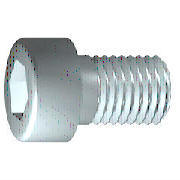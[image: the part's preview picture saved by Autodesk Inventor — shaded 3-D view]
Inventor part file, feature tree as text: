
AUTODESK INVENTOR PART (.ipt)
format: ipt  version: 2020 (Build 240168000, 168)  size: 196,608 bytes
history: native  units: mm (DEFAULTED — no unit token found)
features: sketch x2, other x1, extrude x1, plane x1, fillet x1
ambient origin geometry x7: Origin, YZ Plane, XY Plane, X Axis, Y Axis, Z Axis, Center Point
bodies: Solid1 (feature_tree)
feature tree (6):
  other  "Bryła"
  extrude  "Szczelina"  Depth=11.9mm
  plane  "Work Plane1"
  fillet  "Fillet2"  Radius=0.429515mm
  sketch  "Szkic1"
  sketch  "Szkic2"
